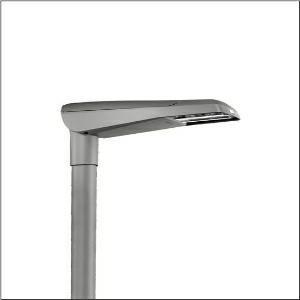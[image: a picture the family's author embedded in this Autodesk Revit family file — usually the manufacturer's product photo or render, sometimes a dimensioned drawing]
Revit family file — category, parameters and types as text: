
# Revit family: streetlight_sl_11_iq_micro___st1_2a_5xc1a61g08ce_6eb0
name_source: partatom
category: Lighting Fixtures
units: mm (PartAtom-declared; Revit-internal decimal feet)

## family parameters
Cut with Voids When Loaded = No
Host = Face
Light Source = No
Part Type = Normal
Room Calculation Point = No
Round Connector Dimension = Use Diameter
Shared = No

## types (1)
- --- (1 x LED, 1690 lm, 12.6 W, 2700K)
    Apparent Load = 13 VA
    CIE Flux Codes = 33 71 96 100 100
    Color Rendering = 70
    Color Temperature = 2700K
    Default Elevation = 1800 mm
    Description = Streetlight SL 11 iQ micro, mast luminaire, primary light control with 3 zone facetted reflector, of plastic, silver coated, highly specular, primary optical cover: cover, of PMMA, transparent, light distribution: ST1.2a, light emission: direct distribution, primary light characteristic: asymmetric, installation type: side-entry, post-top, lamps: LED, High Power LED, rated values: 1.690lm | 12,6W | 134,1lm/W (begin service life); end service life: 1.690lm | 12,9W; at 50% lumin. flux: 845lm | 6,8W | 124,3lm/W, colour temperature: 2700K, colour rendering: CRI > 70, light colour: 727, light setting 1 begin service life: 100% | 1.690lm | 12,6W | 134,1lm/W | 2.700K, light setting 1 end service life: 12,9W, further light settings possible, control: optimised constant luminous flux control (CLO 2.0), Desk-Remote (wireless, voltage-free reading and setting of iQ features in the workshop via application-optimized NFC function/RFID function), Light-Fading, Smart-Wire, Night-Set, Lumen-Switch, Temp-Guard, Auto-Match, Street-Remote, pre-setting: linear dimming characteristic, with cable H07RN-F 5x 1.5mm², mains connection: 230..240V, AC, 50/60Hz, connection cable pre-assembled, cable length: 5,5m, luminaire housing, of diecast aluminium, powder-coated, SITECO metallic grey (DB 702S), please order mast flange separately, inclination adjustable without tools: 0°, 5°, 10°, 15° (post-top) | 0°, -5°, -10°, -15° (side-entry), sealing non-destructively replaceable, multi-level sealing system, length: 600mm, width: 174mm, height: 116mm, mast flange for spigot size: 42mm (side-entry): 5XC10008XM4, 60/48mm (side-entry/post-top): 5XC10108XM2, 76/60mm (side-entry/post-top): 5XC10108XM1, equipment: standard, protection rating (complete): IP66, insulation class (complete): insulation class II (safety insulation), certification: CE, ENEC, ENEC+, VDE, impact resistance: IK10, permissible operating ambient temperature for outdoor applications: -25..+50°C, standard-compliant lighting for roads and squares, Environmental Product Declaration (EPD) tested and certified by an independent institute, packaging unit: 1 piece

Light Distribution: ST1.2a
    Height = 116 mm
    Lamp = 1 x LED
    Lamp Light Flux = 1690 lm
    Lamp Power = 12.6 W
    Lamp count = 1
    Length = 600 mm
    Luminous efficacy = 134 lm/W
    Manufacturer = Siteco
    ModVariant = No
    Model = 5XC1A61G08CE
    Number of Poles = 1
    OnlyDefault = Yes
    Power Factor = 1
    Product Name = Streetlight SL 11 iQ micro | ST1.2a
    Product group = mast luminaire | pylon top
    ProductGroupID = 6100
    Protection Class = Protection class II
    Protection Degree = IP 66
    RLX_Detail_Level = 1
    RLX_Emergency_Light_Flux = 0 lm
    RLX_Emergency_Type = 0
    RLX_Emergency_Type_DB = No
    RlxData = <blob elided: 26537 chars, md5=8dfc0893>
    Socket = socket
    Standby Power = 0 W
    System Light Flux = 1690 lm
    System Power = 13 W
    Type Comments = factory setting: luminous flux: 100 % | dim-lin: 254 | 229 mA
    Type Image = l_1006566.jpg
    URL = http://relux.com
    VarID = @adj_018971
    Voltage = 0 V
    Weight = 0.00 kg
    Width = 174 mm

## geometry (parser evidence)
native form markers: Blend x4, Sweep x13
no freeform markers — native parametric forms only
